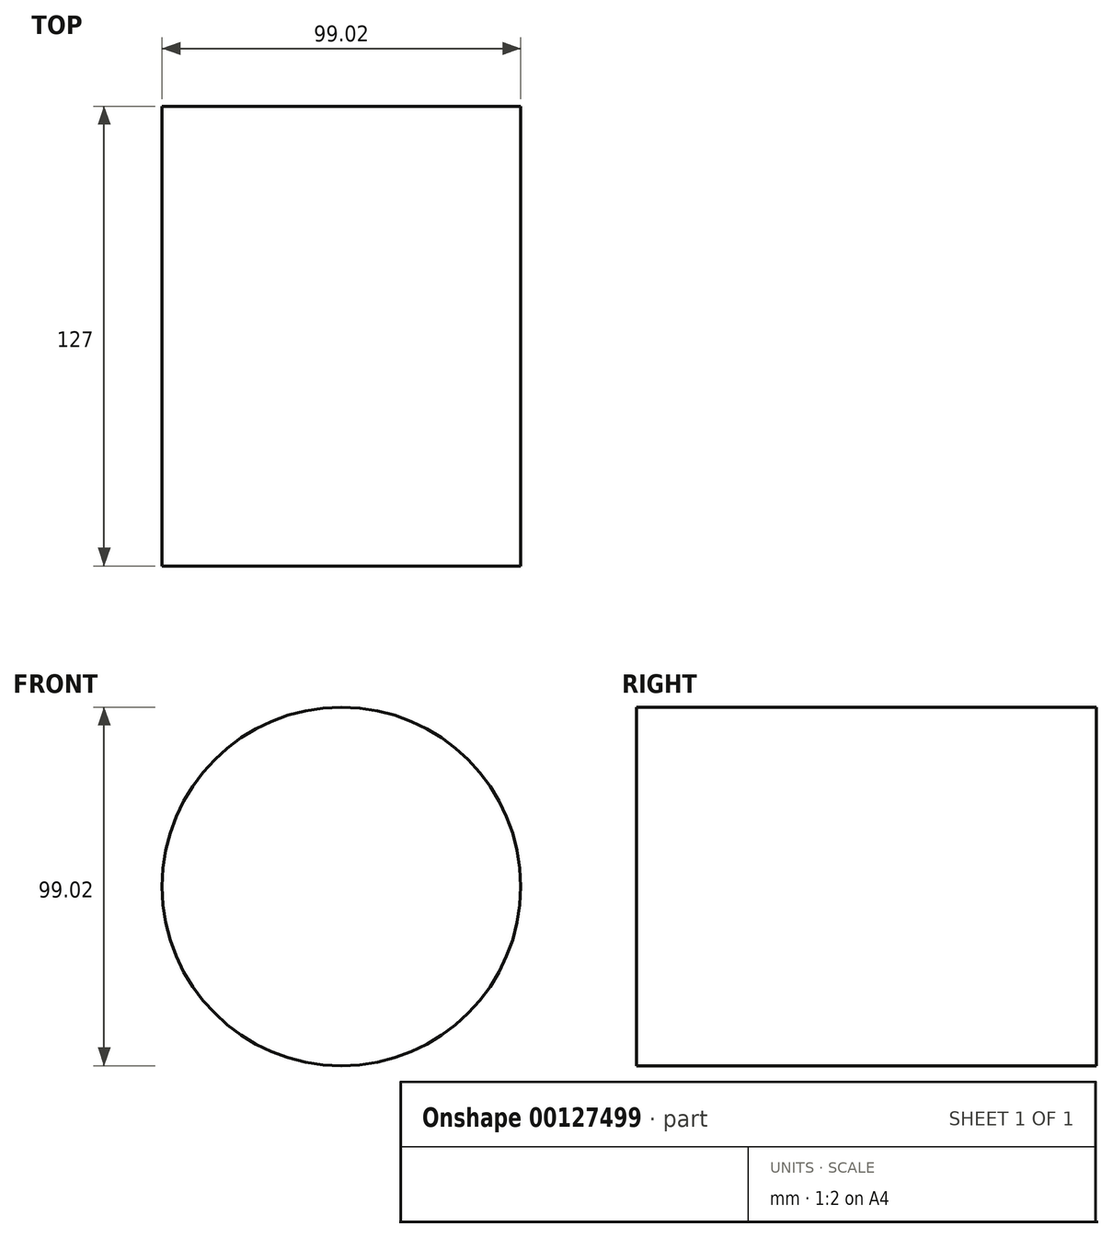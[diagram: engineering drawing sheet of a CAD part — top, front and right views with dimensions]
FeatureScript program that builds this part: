
annotation { "Feature Type Name" : "Feature", "Feature Type Description" : "" }
export const myFeature = defineFeature(function(context is Context, id is Id, definition is map)
    precondition{}
    {
        {
            var Q0;
            Q0=qCreatedBy(makeId("Front.planeOp"),FACE);
            var sketch = newSketch(context, id + "F0", { "sketchPlane" : qUnion([Q0])});
            skCircle(sketch, "E0", {"center": v(0, 0) * mm, "radius": 49.51 * mm});
            skSolve(sketch);
        }
        {
            var Q0;
            Q0=makeQuery(id+"F0.imprint","IMPRINT",FACE,{"disambiguationData":[TD([[makeQuery(id+"F0.imprint","IMPRINT",EDGE,{"derivedFrom":sQuery(id+"F0.wireOp",EDGE,"E0")}),1.0]])]});
            var Q1;
            Q1=sQuery(id+"F0.wireOp",EDGE,"E0");
            extrude(context, id + "F1", {"entities" : qUnion([Q0]), "surfaceEntities" : qUnion([Q1]), "endBound" : BoundingType.SYMMETRIC, "depth" : 127 * mm});
        }
    });
